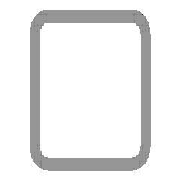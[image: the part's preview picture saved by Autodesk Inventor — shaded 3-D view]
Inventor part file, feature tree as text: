
AUTODESK INVENTOR PART (.ipt)
format: ipt  version: 2022 (Build 260153000, 153)  size: 135,168 bytes
history: native  units: mm (DEFAULTED — no unit token found)
features: other x4, sketch x3, plane x1
ambient origin geometry x8: Origin, YZ Plane, XZ Plane, XY Plane, X Axis, Y Axis, Z Axis, Center Point
bodies: Solid1 (feature_tree), Body (feature_tree)
feature tree (8):
  parser-record x1  (decoder bookkeeping rows leaked as tree rows — omitted from the tree; the rows remain in map.json)
  other  "Driven Length"
  other  "Start Plane"
  other  "End Plane"
  sketch  "Sketch"  dims[d7=7.5mm d10=40.0mm d11=40.0mm d12=5.0mm d13=-0.0mm d14=480.0mm d15=20.0mm d16=20.0mm d17=90.0deg d18=480.0mm]
  sketch  "Sketch3"  dims[d3=480.0mm]
  plane  "Work Plane3"
  sketch  "Sketch4"  dims[d4=0.0mm]
